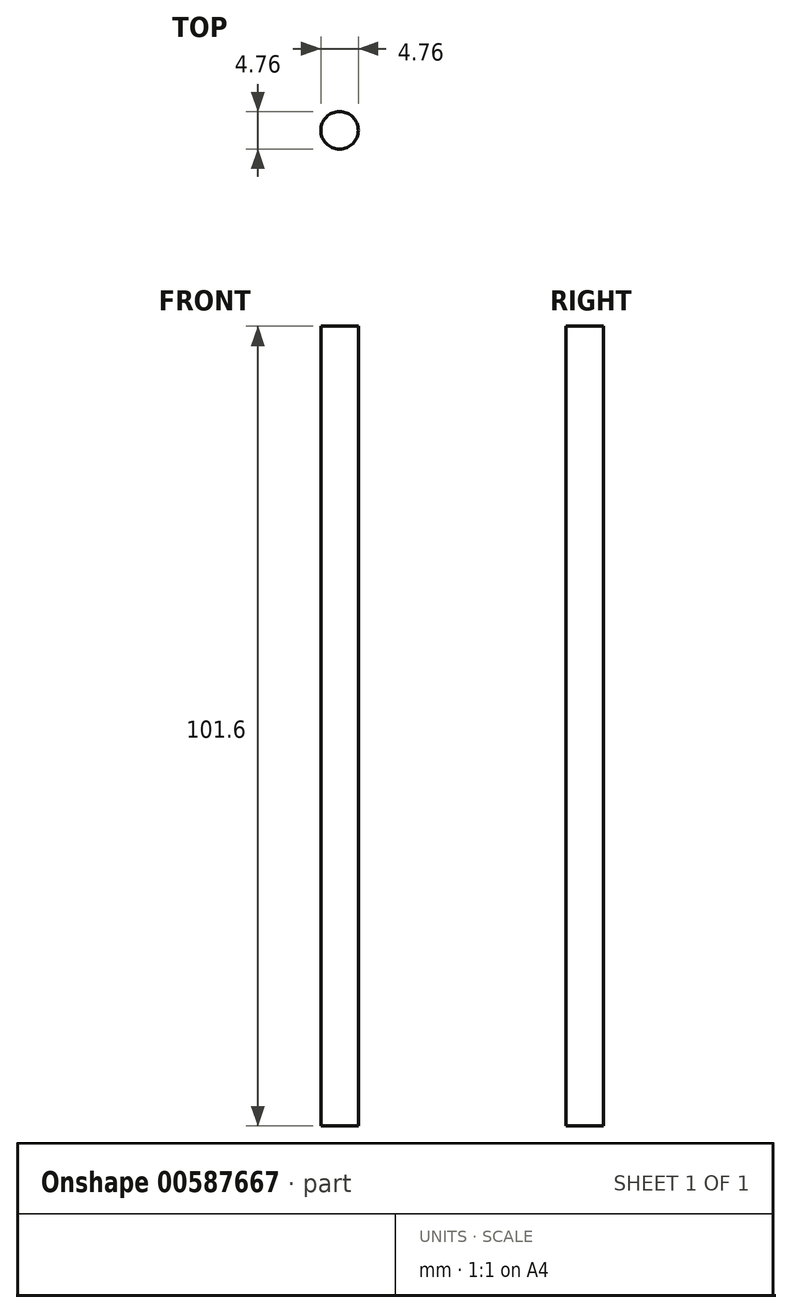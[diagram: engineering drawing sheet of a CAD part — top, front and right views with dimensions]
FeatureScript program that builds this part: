
annotation { "Feature Type Name" : "Feature", "Feature Type Description" : "" }
export const myFeature = defineFeature(function(context is Context, id is Id, definition is map)
    precondition{}
    {
        {
            var Q0;
            Q0=qCreatedBy(makeId("Top.planeOp"),FACE);
            var sketch = newSketch(context, id + "F0", { "sketchPlane" : qUnion([Q0])});
            skCircle(sketch, "E0", {"center": v(0, 0) * mm, "radius": 2.38 * mm});
            skSolve(sketch);
        }
        {
            var Q0;
            Q0 = qSketchRegion(id + "F0", true);
            extrude(context, id + "F1", {"entities" : qUnion([Q0]), "depth" : 101.6 * mm, "offsetDistance" : 25.4 * mm});
        }
    });
